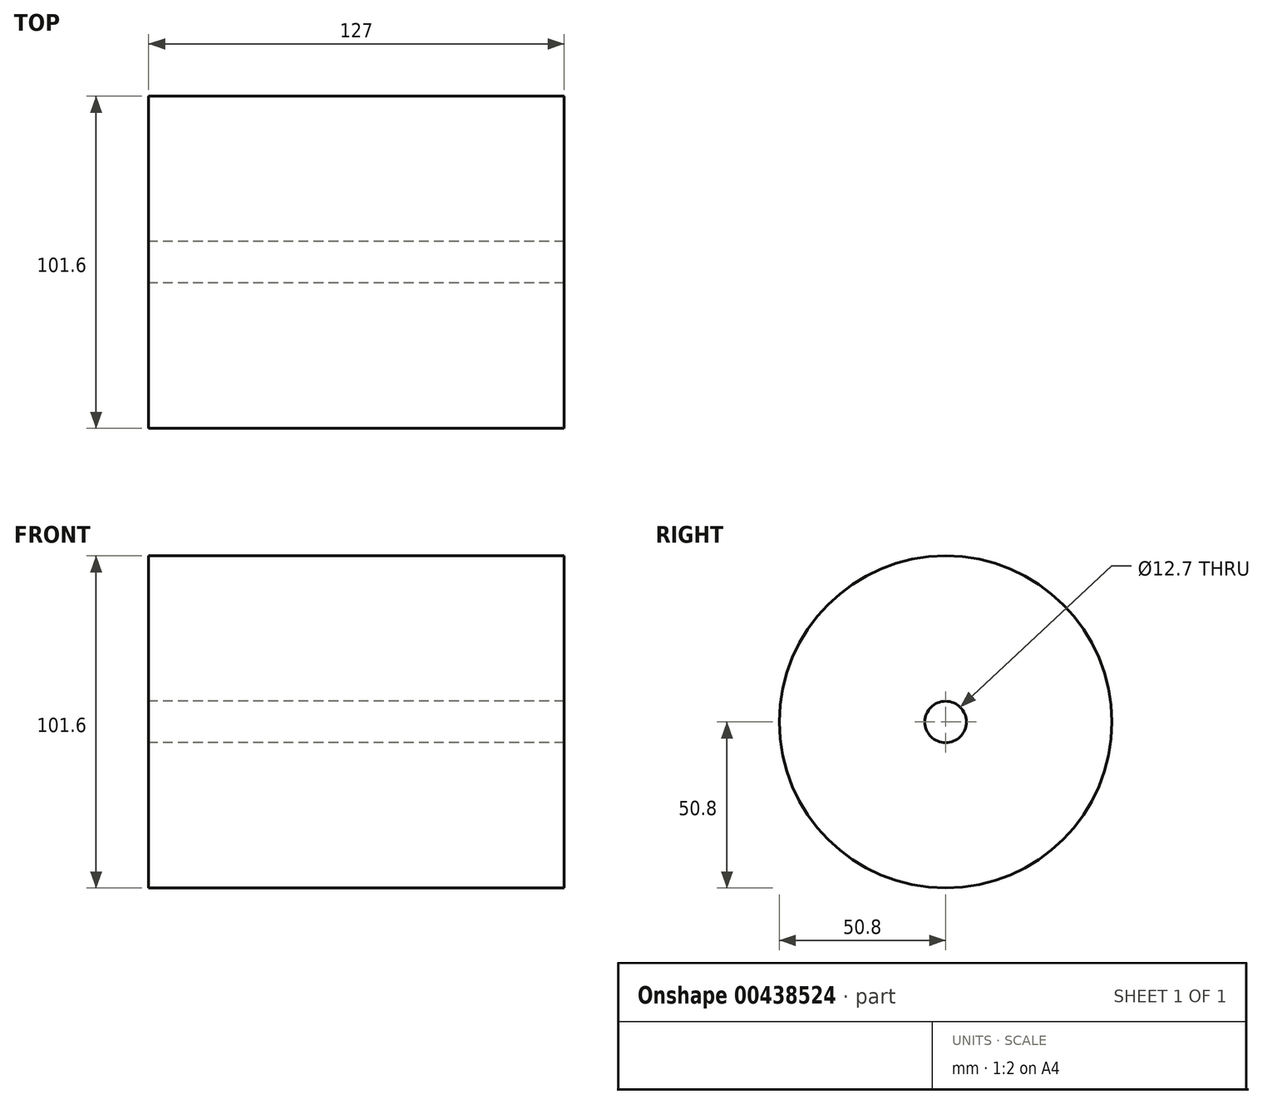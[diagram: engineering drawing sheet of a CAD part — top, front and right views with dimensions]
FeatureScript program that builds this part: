
annotation { "Feature Type Name" : "Feature", "Feature Type Description" : "" }
export const myFeature = defineFeature(function(context is Context, id is Id, definition is map)
    precondition{}
    {
        {
            var Q0;
            Q0=qCreatedBy(makeId("Right.planeOp"),FACE);
            var sketch = newSketch(context, id + "F0", { "sketchPlane" : qUnion([Q0])});
            skCircle(sketch, "E0", {"center": v(0, 0) * mm, "radius": 50.8 * mm});
            skCircle(sketch, "E1", {"center": v(0, 0) * mm, "radius": 6.35 * mm});
            skSolve(sketch);
        }
        {
            var Q0;
            Q0=makeQuery(id+"F0.imprint","IMPRINT",FACE,{"disambiguationData":[TD([[makeQuery(id+"F0.imprint","IMPRINT",EDGE,{"derivedFrom":sQuery(id+"F0.wireOp",EDGE,"E0")}),1.0]])]});
            extrude(context, id + "F1", {"entities" : qUnion([Q0]), "depth" : 127 * mm});
        }
    });
